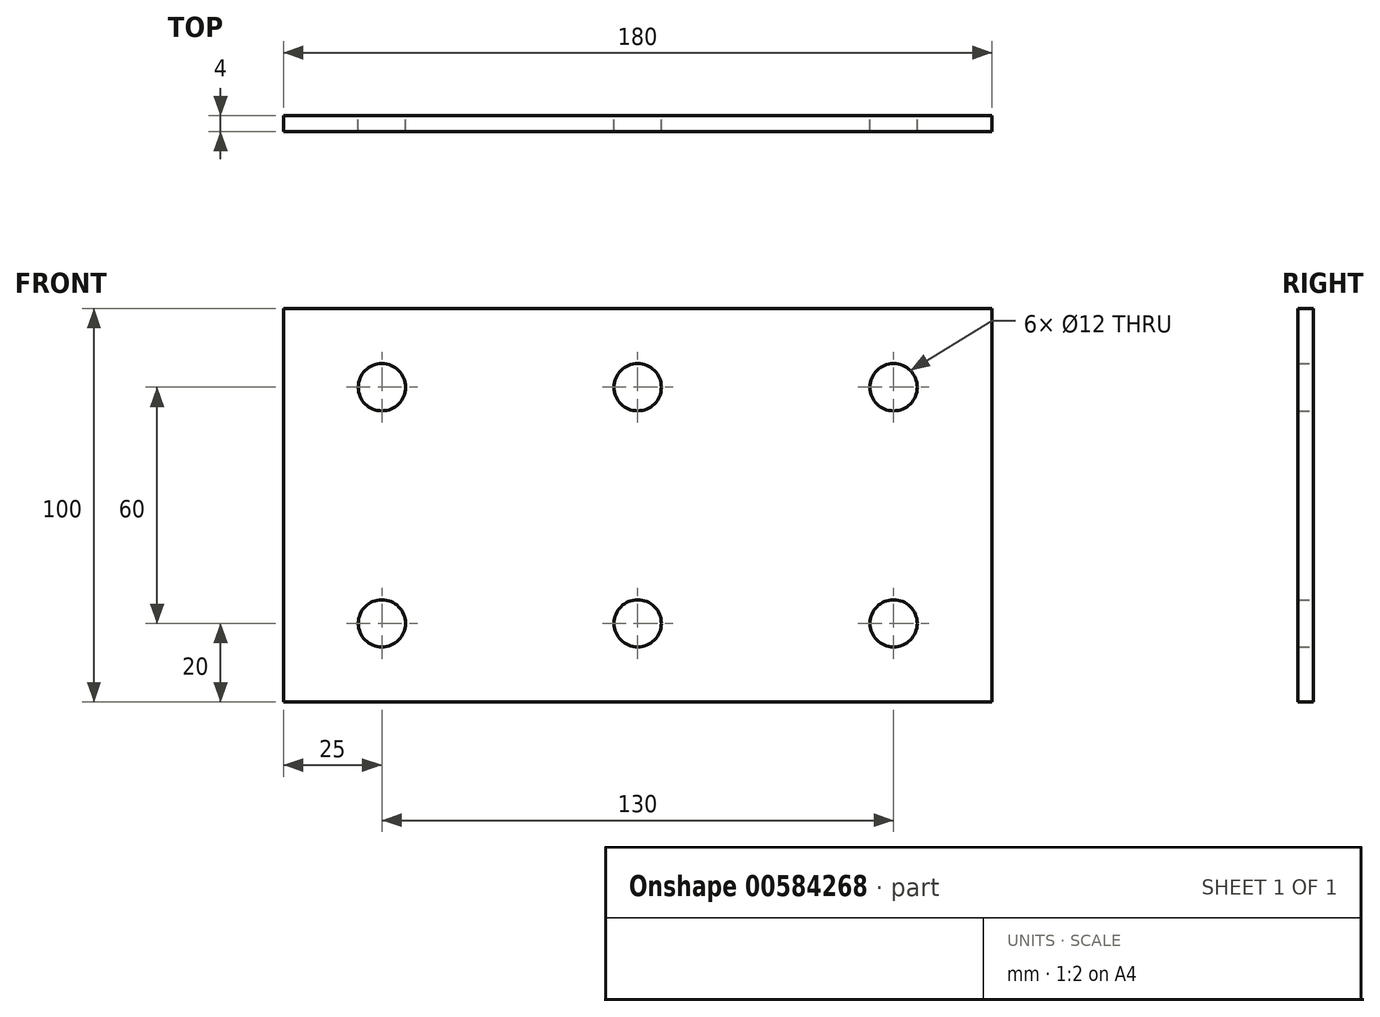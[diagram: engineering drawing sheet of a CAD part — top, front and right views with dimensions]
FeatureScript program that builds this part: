
annotation { "Feature Type Name" : "Feature", "Feature Type Description" : "" }
export const myFeature = defineFeature(function(context is Context, id is Id, definition is map)
    precondition{}
    {
        {
            var Q0;
            Q0=qCreatedBy(makeId("Front.planeOp"),FACE);
            var sketch = newSketch(context, id + "F0", { "sketchPlane" : qUnion([Q0])});
            skLineSegment(sketch, "E0.bottom", {"start": v(0, 0) * mm, "end": v(180, 0) * mm});
            skLineSegment(sketch, "E0.top", {"start": v(0, 100) * mm, "end": v(180, 100) * mm});
            skLineSegment(sketch, "E0.left", {"start": v(0, 0) * mm, "end": v(0, 100) * mm});
            skLineSegment(sketch, "E0.right", {"start": v(180, 0) * mm, "end": v(180, 100) * mm});
            skSolve(sketch);
        }
        {
            var Q0;
            Q0=makeQuery(id+"F0.imprint","IMPRINT",FACE,{"disambiguationData":[TD([[makeQuery(id+"F0.imprint","IMPRINT",EDGE,{"derivedFrom":sQuery(id+"F0.wireOp",EDGE,"E0.bottom")}),1.0]])]});
            extrude(context, id + "F1", {"entities" : qUnion([Q0]), "depth" : 4 * mm, "offsetDistance" : 25 * mm});
        }
        {
            var Q0;
            Q0=qCreatedBy(makeId("Front.planeOp"),FACE);
            var sketch = newSketch(context, id + "F2", { "sketchPlane" : qUnion([Q0])});
            skCircle(sketch, "E1", {"center": v(25, 80) * mm, "radius": 6 * mm});
            skSolve(sketch);
        }
        {
            var Q0;
            Q0=makeQuery(id+"F1.opExtrude","CAP_FACE",FACE,{"disambiguationData":[OSD([sQuery(id+"F0.wireOp",EDGE,"E0.bottom"),sQuery(id+"F0.wireOp",EDGE,"E0.top"),sQuery(id+"F0.wireOp",EDGE,"E0.left"),sQuery(id+"F0.wireOp",EDGE,"E0.right")])],"isStart":true});
            var sketch = newSketch(context, id + "F3", { "sketchPlane" : qUnion([Q0])});
            skCircle(sketch, "E2", {"center": v(-155, 20) * mm, "radius": 6 * mm});
            skCircle(sketch, "E3", {"center": v(-155, 80) * mm, "radius": 6 * mm});
            skCircle(sketch, "E4", {"center": v(-25, 20) * mm, "radius": 6 * mm});
            skCircle(sketch, "E5", {"center": v(-90, 80) * mm, "radius": 6 * mm});
            skCircle(sketch, "E6", {"center": v(-90, 20) * mm, "radius": 6 * mm});
            skSolve(sketch);
        }
        {
            var Q0;
            Q0 = qSketchRegion(id + "F2", true);
            var Q1;
            Q1 = qSketchRegion(id + "F3", true);
            var Q2;
            Q2 = qConstructionFilter(qBodyType(qCreatedBy(id + "F2" ,EDGE), BodyType.WIRE), ConstructionObject.NO);
            var Q3;
            Q3 = qConstructionFilter(qBodyType(qCreatedBy(id + "F3" ,EDGE), BodyType.WIRE), ConstructionObject.NO);
            extrude(context, id + "F4", {"entities" : qUnion([Q0, Q1]), "operationType" : NewBodyOperationType.REMOVE, "surfaceEntities" : qUnion([Q2, Q3]), "depth" : 100 * mm, "offsetDistance" : 25 * mm});
        }
    });
